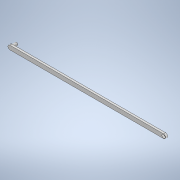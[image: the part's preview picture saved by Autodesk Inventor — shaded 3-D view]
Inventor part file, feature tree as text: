
AUTODESK INVENTOR PART (.ipt)
format: ipt  version: 2021 (Build 250183000, 183)  size: 110,080 bytes
history: native  units: in
note: dims shown in document units (in); Inventor stores cm internally (conversion verified against a paired STEP export)
features: extrude x3, sketch x3, other x1
ambient origin geometry x8: Origin, YZ Plane, XZ Plane, XY Plane, X Axis, Y Axis, Z Axis, Center Point
bodies: Body1 (feature_tree)
feature tree (7):
  other  "Sólido1"
  extrude  "Extrusión1"  Depth=0.25in
  extrude  "Extrusión2"  Depth=0.2756in TaperAngle=0.0deg
  extrude  "Extrusión3"  Depth=0.25in
  sketch  "Boceto1"  dims[d0=0.25in d3=0.25in]
  sketch  "Boceto2"  dims[d4=0.125in d5=0.0in d8=0.2756in d9=0.0in]
  sketch  "Boceto3"  dims[d10=0.25in d11=0.0197in d12=0.1969in d13=0.0in d14=19.685in d15=0.0344in]
